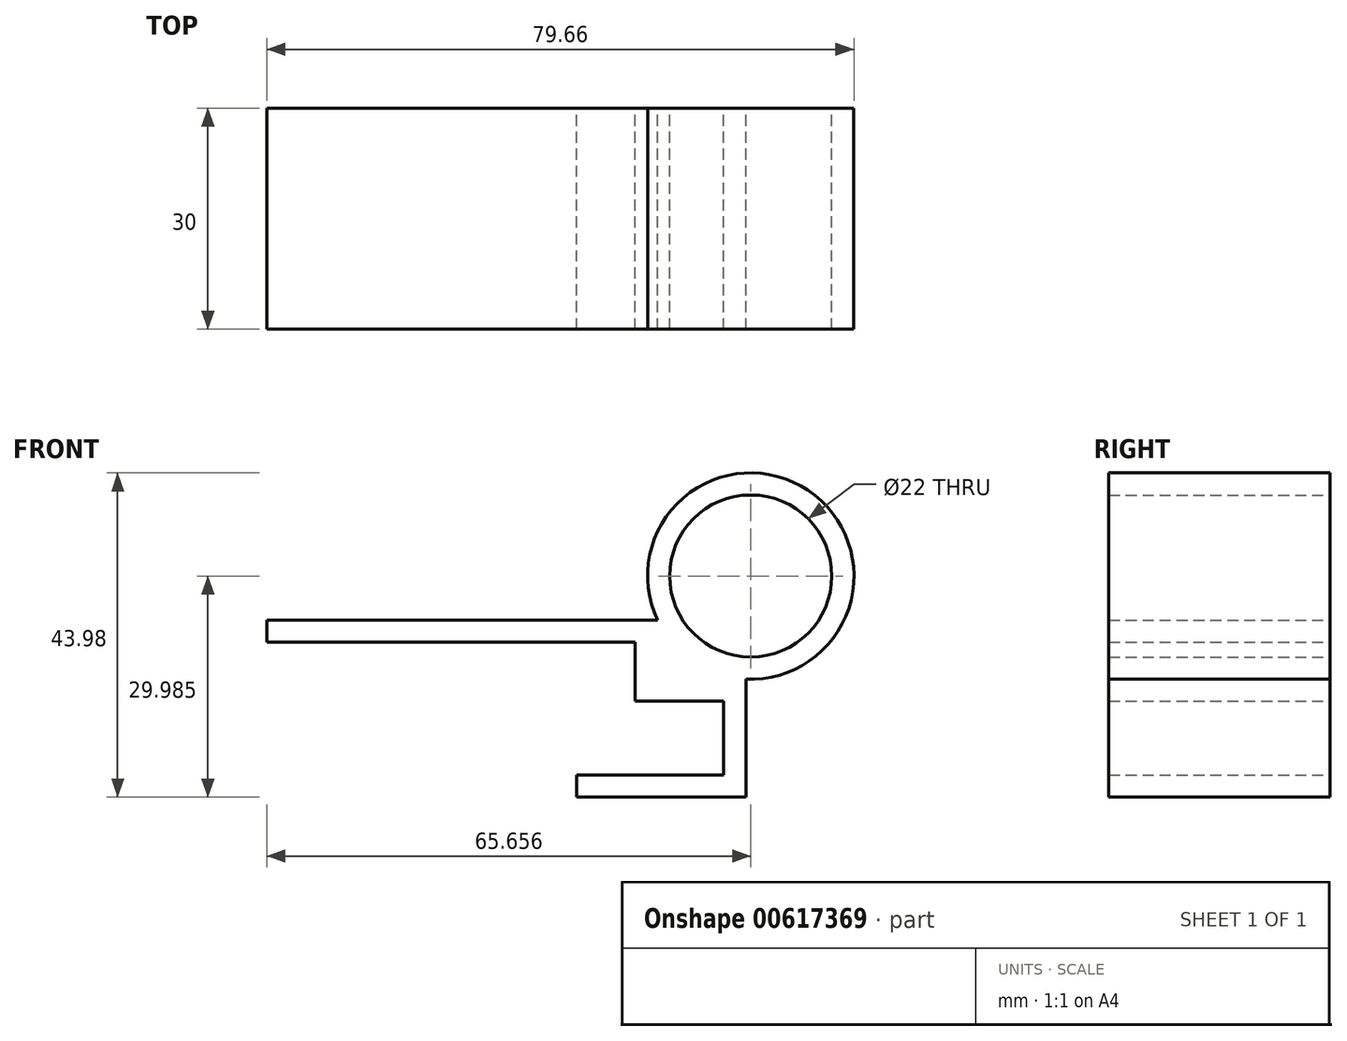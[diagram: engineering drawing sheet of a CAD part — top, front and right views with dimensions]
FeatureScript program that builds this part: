
annotation { "Feature Type Name" : "Feature", "Feature Type Description" : "" }
export const myFeature = defineFeature(function(context is Context, id is Id, definition is map)
    precondition{}
    {
        {
            var Q0;
            Q0=qCreatedBy(makeId("Front.planeOp"),FACE);
            var sketch = newSketch(context, id + "F0", { "sketchPlane" : qUnion([Q0])});
            skLineSegment(sketch, "E0.bottom", {"start": v(0, 0) * mm, "end": v(50, 0) * mm});
            skLineSegment(sketch, "E0.top", {"start": v(0, 3) * mm, "end": v(50, 3) * mm});
            skLineSegment(sketch, "E0.right", {"start": v(50, 0) * mm, "end": v(50, 3) * mm});
            skLineSegment(sketch, "E1.bottom", {"start": v(50, 3) * mm, "end": v(53, 3) * mm});
            skLineSegment(sketch, "E1.top", {"start": v(50, -8) * mm, "end": v(53, -8) * mm});
            skLineSegment(sketch, "E1.left", {"start": v(50, 3) * mm, "end": v(50, -8) * mm});
            skLineSegment(sketch, "E1.right", {"start": v(53, 3) * mm, "end": v(53, -8) * mm});
            skPoint(sketch, "E2", {"position": v(53, 0) * mm});
            skLineSegment(sketch, "E3.bottom", {"start": v(50, -8) * mm, "end": v(65, -8) * mm});
            skLineSegment(sketch, "E3.top", {"start": v(50, -5) * mm, "end": v(65, -5) * mm});
            skLineSegment(sketch, "E3.left", {"start": v(50, -8) * mm, "end": v(50, -5) * mm});
            skLineSegment(sketch, "E3.right", {"start": v(65, -8) * mm, "end": v(65, -5) * mm});
            skPoint(sketch, "E4", {"position": v(53, -5) * mm});
            skLineSegment(sketch, "E5.bottom", {"start": v(65, -5) * mm, "end": v(62, -5) * mm});
            skLineSegment(sketch, "E5.top", {"start": v(65, -18) * mm, "end": v(62, -18) * mm});
            skLineSegment(sketch, "E5.left", {"start": v(65, -5) * mm, "end": v(65, -18) * mm});
            skLineSegment(sketch, "E5.right", {"start": v(62, -5) * mm, "end": v(62, -18) * mm});
            skLineSegment(sketch, "E6.bottom", {"start": v(65, -18) * mm, "end": v(42, -18) * mm});
            skLineSegment(sketch, "E6.top", {"start": v(65, -21) * mm, "end": v(42, -21) * mm});
            skLineSegment(sketch, "E6.left", {"start": v(65, -18) * mm, "end": v(65, -21) * mm});
            skLineSegment(sketch, "E6.right", {"start": v(42, -18) * mm, "end": v(42, -21) * mm});
            skPoint(sketch, "E7", {"position": v(62, -8) * mm});
            skLineSegment(sketch, "E8", {"start": v(0, 3) * mm, "end": v(0, 0) * mm});
            skCircle(sketch, "E9", {"center": v(65.66, 8.98) * mm, "radius": 11 * mm});
            skCircle(sketch, "E10", {"center": v(65.66, 8.98) * mm, "radius": 14 * mm});
            skSolve(sketch);
        }
        {
            var Q0;
            Q0=qSketchRegion(id+"F0",true);
            extrude(context, id + "F1", {"entities" : qUnion([Q0]), "depth" : 15 * mm, "hasSecondDirection" : true, "secondDirectionOppositeDirection" : true, "secondDirectionDepth" : 15 * mm, "offsetDistance" : 25 * mm});
        }
    });
